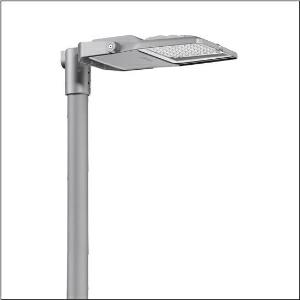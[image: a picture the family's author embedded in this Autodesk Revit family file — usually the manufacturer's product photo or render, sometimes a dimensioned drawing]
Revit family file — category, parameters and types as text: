
# Revit family: floodlight_fl_21_iq_mini___pl43_5xa7772b2a3a_a256
name_source: partatom
category: Lighting Fixtures
units: mm (PartAtom-declared; Revit-internal decimal feet)

## family parameters
Cut with Voids When Loaded = No
Host = Face
Light Source = No
Part Type = Normal
Room Calculation Point = No
Round Connector Dimension = Use Diameter
Shared = No

## types (1)
- --- (1 x LED, 6400 lm, 45.5 W, 3000K)
    Apparent Load = 46 VA
    CIE Flux Codes = 27 78 99 100 100
    Color Rendering = 70
    Color Temperature = 3000K
    Default Elevation = 1800 mm
    Description = Floodlight FL 21 iQ mini, floodlight, primary light control with lens, of PMMA, primary optical cover: protective disc, of toughened safety glass, transparent, light distribution: PL43, light emission: direct distribution, installation type: surface-mounted, LED, High Power LED, rated luminous flux: 6.400lm, luminous efficacy: 141lm/W, light colour: 730, colour temperature: 3000K, control: Auto-Match, Temp-Guard, Night-Set, Smart-Wire, Desk-Remote (wireless, voltage-free reading and setting of iQ features in the workshop via application-optimized NFC function/RFID function), optimised constant luminous flux control (CLO 2.0), Light-Fading, Lumen-Switch, with terminal, 6-pole, mains connection: 220..240V, AC, 50/60Hz, start of lifetime: 46W, end of service life: 48W, reduction: 22W, luminaire housing, of diecast aluminium, powder-coated, Siteco® metallic grey (DB 702S), corrosivity category C5 mid according to DIN EN ISO 12944, sealing non-destructively replaceable, please order mast flange separately, mast bracket, of steel, galvanised, powder-coated, protection rating (complete): IP66, insulation class (complete): insulation class II (safety insulation), certification: CE, ENEC, VDE, protection symbol: D, impact resistance: IK08, permissible operating ambient temperature: -40..+40°C, permissible operating ambient temperature for outdoor applications: -40..+50°C, standard: DIN EN 12944, LABS conformity tested according to VDMA 24364:2018-05, packaging unit: 1 piece

Light Distribution: PL43
    Height = 70 mm
    Lamp = 1 x LED
    Lamp Light Flux = 6400 lm
    Lamp Power = 45.5 W
    Lamp count = 1
    Length = 485 mm
    Luminous efficacy = 141 lm/W
    Manufacturer = Siteco
    ModVariant = No
    Model = 5XA7772B2A3A
    Number of Poles = 1
    OnlyDefault = Yes
    Power Factor = 1
    Product Name = Floodlight FL 21 iQ mini | PL43
    Product group = floodlight | pylon annexe
    ProductGroupID = 6200
    Protection Class = Protection class II
    Protection Degree = IP 66
    RLX_Detail_Level = 1
    RLX_Emergency_Light_Flux = 0 lm
    RLX_Emergency_Type = 0
    RLX_Emergency_Type_DB = No
    RlxData = <blob elided: 100961 chars, md5=a505714f>
    Socket = socket
    Standby Power = 0 W
    System Light Flux = 6400 lm
    System Power = 46 W
    Type Comments = factory setting: luminous flux: 100 % | dim-lin: 254 | 463 mA
    Type Image = l_1007125.jpg
    URL = http://relux.com
    VarID = @adj_095089
    Voltage = 0 V
    Weight = 0.00 kg
    Width = 337 mm

## geometry (parser evidence)
native form markers: Blend x4, Sweep x11
no freeform markers — native parametric forms only
